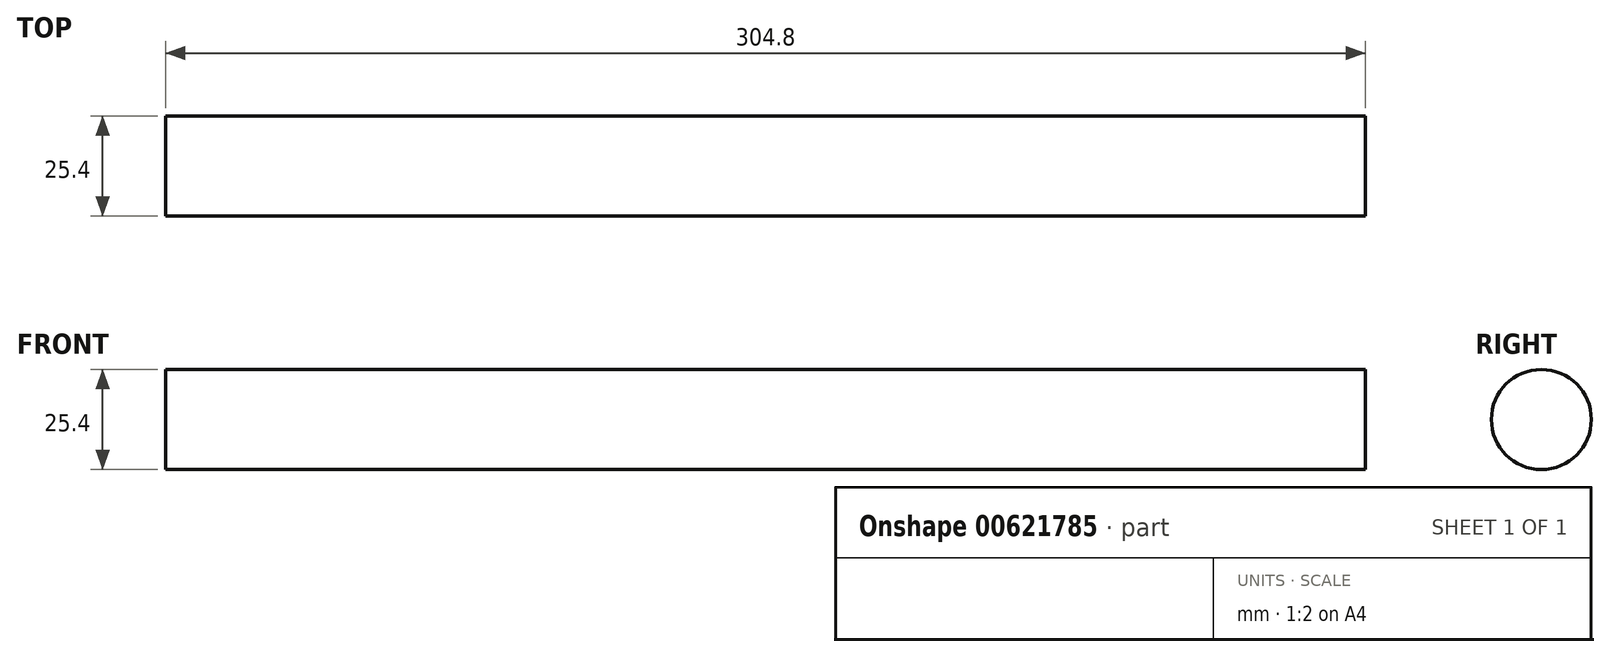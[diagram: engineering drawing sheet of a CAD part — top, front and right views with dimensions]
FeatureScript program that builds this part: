
annotation { "Feature Type Name" : "Feature", "Feature Type Description" : "" }
export const myFeature = defineFeature(function(context is Context, id is Id, definition is map)
    precondition{}
    {
        {
            var Q0;
            Q0=qCreatedBy(makeId("Right.planeOp"),FACE);
            var sketch = newSketch(context, id + "F0", { "sketchPlane" : qUnion([Q0])});
            skCircle(sketch, "E0", {"center": v(0, 0) * mm, "radius": 12.7 * mm});
            skSolve(sketch);
        }
        {
            var Q0;
            Q0=makeQuery(id+"F0.imprint","IMPRINT",FACE,{"disambiguationData":[TD([[makeQuery(id+"F0.imprint","IMPRINT",EDGE,{"derivedFrom":sQuery(id+"F0.wireOp",EDGE,"E0")}),1.0]])]});
            extrude(context, id + "F1", {"entities" : qUnion([Q0]), "depth" : 304.8 * mm, "offsetDistance" : 25.4 * mm});
        }
    });
